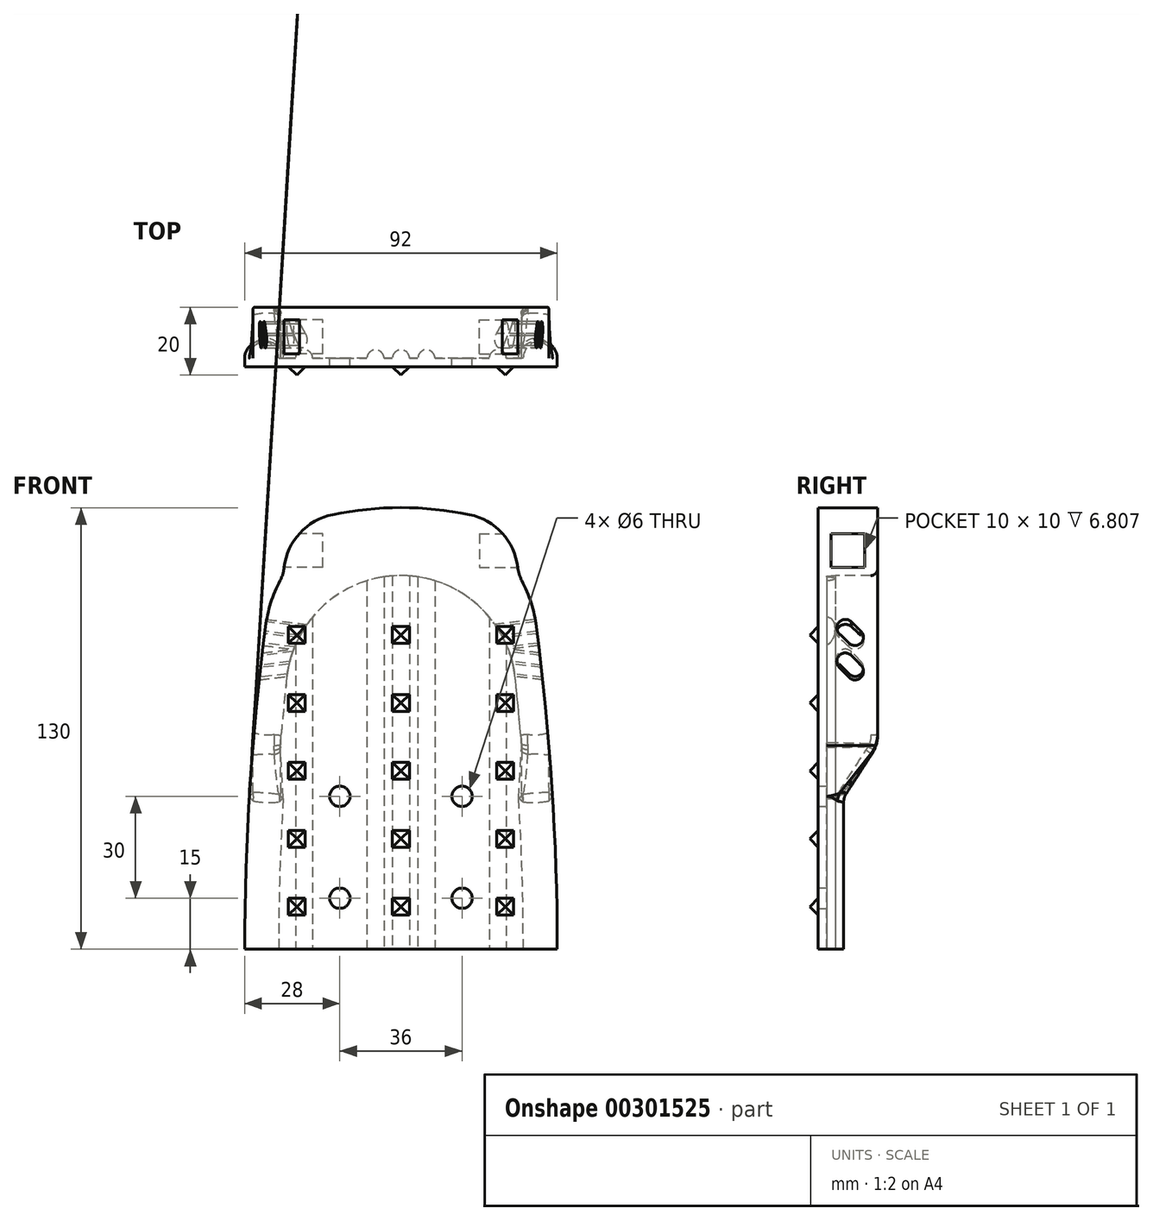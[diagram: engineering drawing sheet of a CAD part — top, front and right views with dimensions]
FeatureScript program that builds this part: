
annotation { "Feature Type Name" : "Feature", "Feature Type Description" : "" }
export const myFeature = defineFeature(function(context is Context, id is Id, definition is map)
    precondition{}
    {
        {
            assignVariable(context, id + "F0", {"name" : "Tb", "anyValue" : 2.5});
        }
        {
            assignVariable(context, id + "F1", {"name" : "tb2", "anyValue" : 15});
        }
        {
            var Q0;
            Q0=qCreatedBy(makeId("Front.planeOp"),FACE);
            var sketch = newSketch(context, id + "F2", { "sketchPlane" : qUnion([Q0])});
            skLineSegment(sketch, "E0", {"start": v(0, 0) * mm, "end": v(0, 130) * mm, "construction": true});
            skLineSegment(sketch, "E1", {"start": v(0, 0) * mm, "end": v(-41, 0) * mm});
            skLineSegment(sketch, "E2", {"start": v(0, 0) * mm, "end": v(46, 0) * mm});
            skLineSegment(sketch, "E3", {"start": v(0, 16) * mm, "end": v(-42, 16) * mm, "construction": true});
            skLineSegment(sketch, "E4", {"start": v(0, 16) * mm, "end": v(61, 16) * mm, "construction": true});
            skLineSegment(sketch, "E5", {"start": v(61, 26) * mm, "end": v(0, 26) * mm, "construction": true});
            skLineSegment(sketch, "E6", {"start": v(0, 26) * mm, "end": v(-43, 26) * mm, "construction": true});
            skLineSegment(sketch, "E7", {"start": v(-42, 46) * mm, "end": v(0, 46) * mm, "construction": true});
            skLineSegment(sketch, "E8", {"start": v(0, 46) * mm, "end": v(60, 46) * mm, "construction": true});
            skLineSegment(sketch, "E9", {"start": v(-40, 71) * mm, "end": v(0, 71) * mm, "construction": true});
            skLineSegment(sketch, "E10", {"start": v(0, 71) * mm, "end": v(53, 71) * mm, "construction": true});
            skLineSegment(sketch, "E11", {"start": v(-35, 97) * mm, "end": v(0, 97) * mm, "construction": true});
            skLineSegment(sketch, "E12", {"start": v(0, 97) * mm, "end": v(44, 97) * mm, "construction": true});
            skLineSegment(sketch, "E13", {"start": v(-29, 112) * mm, "end": v(0, 112) * mm, "construction": true});
            skLineSegment(sketch, "E14", {"start": v(0, 112) * mm, "end": v(35, 112) * mm, "construction": true});
            skArc(sketch, "E15", {"start": v(39.87, 94.96) * mm, "mid": v(26.54, 120) * mm, "end": v(0, 130) * mm});
            skPoint(sketch, "E16.visualSharp", {"position": v(-35, 97) * mm});
            skPoint(sketch, "E17.visualSharp", {"position": v(-40, 71) * mm});
            skPoint(sketch, "E18.visualSharp", {"position": v(-42, 46) * mm});
            skPoint(sketch, "E19.visualSharp", {"position": v(-43, 26) * mm});
            skPoint(sketch, "E20.visualSharp", {"position": v(-42, 16) * mm});
            skPoint(sketch, "E21.visualSharp", {"position": v(61, 16) * mm});
            skPoint(sketch, "E22.visualSharp", {"position": v(61, 26) * mm});
            skPoint(sketch, "E23.visualSharp", {"position": v(60, 46) * mm});
            skPoint(sketch, "E24.visualSharp", {"position": v(53, 71) * mm});
            skPoint(sketch, "E25.visualSharp", {"position": v(44, 97) * mm});
            skArc(sketch, "E26", {"start": v(46, 0) * mm, "mid": v(44.47, 47.58) * mm, "end": v(39.87, 94.96) * mm});
            skLineSegment(sketch, "E27", {"start": v(-41, 0) * mm, "end": v(-46, 0) * mm});
            skLineSegment(sketch, "E28", {"start": v(46, 0) * mm, "end": v(46, 0) * mm});
            skLineSegment(sketch, "E29", {"start": v(-27.54, 130) * mm, "end": v(25.43, 130) * mm, "construction": true});
            skArc(sketch, "E30.MirrorCS", {"start": v(-39.87, 94.96) * mm, "mid": v(-26.54, 120) * mm, "end": v(0, 130) * mm});
            skArc(sketch, "E31.MirrorCS", {"start": v(-46, 0) * mm, "mid": v(-44.47, 47.58) * mm, "end": v(-39.87, 94.96) * mm});
            skLineSegment(sketch, "E32", {"start": v(46, 0) * mm, "end": v(46, -31.18) * mm, "construction": true});
            skLineSegment(sketch, "E33", {"start": v(-80.2, 90) * mm, "end": v(120.58, 90) * mm, "construction": true});
            skPoint(sketch, "E34", {"position": v(40.5, 90) * mm});
            skSolve(sketch);
        }
        {
            var Q0;
            Q0=qSketchRegion(id+"F2",true);
            var Q1;
            {var subQ5=sQuery(id+"F2.wireOp",EDGE,"E4");Q1=makeQuery(id+"F2.imprint","IMPRINT",FACE,{"disambiguationData":[TD([[makeQuery(id+"F2.imprint","IMPRINT",EDGE,{"derivedFrom":subQ5}),1.0]])]});}
            var Q2;
            {var subQ2=sQuery(id+"F2.wireOp",EDGE,"E14");Q2=makeQuery(id+"F2.imprint","IMPRINT",FACE,{"disambiguationData":[TD([[makeQuery(id+"F2.imprint","IMPRINT",EDGE,{"derivedFrom":subQ2}),1.0]])]});}
            var Q3;
            {var subQ2=sQuery(id+"F2.wireOp",EDGE,"E13");Q3=makeQuery(id+"F2.imprint","IMPRINT",FACE,{"disambiguationData":[TD([[makeQuery(id+"F2.imprint","IMPRINT",EDGE,{"derivedFrom":subQ2}),1.0]])]});}
            var Q4;
            {var subQ5=sQuery(id+"F2.wireOp",EDGE,"E3");Q4=makeQuery(id+"F2.imprint","IMPRINT",FACE,{"disambiguationData":[TD([[makeQuery(id+"F2.imprint","IMPRINT",EDGE,{"derivedFrom":subQ5}),-1.0]])]});}
            var Q5;
            {var subQ0=sQuery(id+"F2.wireOp",EDGE,"E9");var subQ1=sQuery(id+"F2.wireOp",EDGE,"E0");var subQ2=makeQuery(id+"F2.imprint","INTERSECT",VERTEX,{"derivedFrom":[subQ1,subQ0]});Q5=makeQuery(id+"F2.imprint","IMPRINT",FACE,{"disambiguationData":[TD([[makeQuery(id+"F2.imprint","IMPRINT",EDGE,{"disambiguationData":[TD([[subQ2,-1.0]])],"derivedFrom":subQ1}),1.0]])]});}
            var Q6;
            {var subQ3=sQuery(id+"F2.wireOp",EDGE,"E13");Q6=makeQuery(id+"F2.imprint","IMPRINT",FACE,{"disambiguationData":[TD([[makeQuery(id+"F2.imprint","IMPRINT",EDGE,{"derivedFrom":subQ3}),-1.0]])]});}
            var Q7;
            {var subQ1=sQuery(id+"F2.wireOp",EDGE,"E0");var subQ5=makeQuery(id+"F2.imprint","IMPRINT",VERTEX,{"derivedFrom":subQ1});Q7=makeQuery(id+"F2.imprint","IMPRINT",FACE,{"disambiguationData":[TD([[makeQuery(id+"F2.imprint","IMPRINT",EDGE,{"disambiguationData":[TD([[subQ5,1.0]])],"derivedFrom":subQ1}),1.0]])]});}
            extrude(context, id + "F3", {"entities" : qUnion([Q0, Q1, Q2, Q3, Q4, Q5, Q6, Q7]), "depth" : (getVariable(context, 'Tb')) * mm});
        }
        {
            var Q0;
            Q0=makeQuery(id+"F3.opExtrude","CAP_FACE",FACE,{"disambiguationData":[OSD([sQuery(id+"F2.wireOp",EDGE,"E1"),sQuery(id+"F2.wireOp",EDGE,"E2"),sQuery(id+"F2.wireOp",EDGE,"E15"),sQuery(id+"F2.wireOp",EDGE,"E26"),sQuery(id+"F2.wireOp",EDGE,"E27"),sQuery(id+"F2.wireOp",EDGE,"E30.MirrorCS"),sQuery(id+"F2.wireOp",EDGE,"E31.MirrorCS")])],"isStart":true});
            var sketch = newSketch(context, id + "F4", { "sketchPlane" : qUnion([Q0])});
            skArc(sketch, "E35.0", {"start": v(39.87, 94.96) * mm, "mid": v(0, 130) * mm, "end": v(-39.87, 94.96) * mm});
            skArc(sketch, "E36.0", {"start": v(-43.56, 60) * mm, "mid": v(-41.93, 77.5) * mm, "end": v(-39.87, 94.96) * mm});
            skArc(sketch, "E37.0", {"start": v(43.56, 60) * mm, "mid": v(41.93, 77.5) * mm, "end": v(39.87, 94.96) * mm});
            skPoint(sketch, "E38", {"position": v(0, 130) * mm});
            skArc(sketch, "E39.0", {"start": v(-35.53, 60) * mm, "mid": v(-34.65, 69.94) * mm, "end": v(-33.62, 79.87) * mm});
            skArc(sketch, "E40.0", {"start": v(35.53, 60) * mm, "mid": v(34.65, 69.94) * mm, "end": v(33.62, 79.87) * mm});
            skArc(sketch, "E41", {"start": v(33.62, 79.87) * mm, "mid": v(0, 110) * mm, "end": v(-33.62, 79.87) * mm});
            skPoint(sketch, "E42", {"position": v(0, 110) * mm});
            skLineSegment(sketch, "E43", {"start": v(-43.56, 60) * mm, "end": v(-35.53, 60) * mm});
            skLineSegment(sketch, "E44", {"start": v(35.53, 60) * mm, "end": v(43.56, 60) * mm});
            skSolve(sketch);
        }
        {
            var Q0;
            Q0 = qSketchRegion(id + "F4", true);
            extrude(context, id + "F5", {"entities" : qUnion([Q0]), "operationType" : NewBodyOperationType.ADD, "depth" : (getVariable(context, 'tb2')) * mm});
        }
        {
            var Q0;
            Q0=makeQuery(id+"F5.opExtrude","CAP_FACE",FACE,{"disambiguationData":[OSD([sQuery(id+"F4.wireOp",EDGE,"E35.0"),sQuery(id+"F4.wireOp",EDGE,"E36.0"),sQuery(id+"F4.wireOp",EDGE,"E37.0"),sQuery(id+"F4.wireOp",EDGE,"E39.0"),sQuery(id+"F4.wireOp",EDGE,"E40.0"),sQuery(id+"F4.wireOp",EDGE,"E41"),sQuery(id+"F4.wireOp",EDGE,"E43"),sQuery(id+"F4.wireOp",EDGE,"E44")])],"isStart":false});
            var sketch = newSketch(context, id + "F6", { "sketchPlane" : qUnion([Q0])});
            skLineSegment(sketch, "E45", {"start": v(0, 0) * mm, "end": v(0, 130) * mm, "construction": true});
            skArc(sketch, "E46.0", {"start": v(39.87, 94.96) * mm, "mid": v(0, 130) * mm, "end": v(-39.87, 94.96) * mm});
            skPoint(sketch, "E47", {"position": v(-33.06, 117.38) * mm});
            skPoint(sketch, "E48", {"position": v(33.06, 117.38) * mm});
            skPoint(sketch, "E49", {"position": v(0, 65) * mm});
            skArc(sketch, "E50", {"start": v(-20.12, 127.95) * mm, "mid": v(-29.78, 122.48) * mm, "end": v(-34.38, 112.38) * mm});
            skArc(sketch, "E51", {"start": v(0, 130) * mm, "mid": v(-10.11, 129.49) * mm, "end": v(-20.12, 127.95) * mm});
            skLineSegment(sketch, "E52", {"start": v(-37.94, 130) * mm, "end": v(-5.5, 130) * mm, "construction": true});
            skPoint(sketch, "E53", {"position": v(0, 130) * mm});
            skArc(sketch, "E54.MirrorCS", {"start": v(0, 130) * mm, "mid": v(10.11, 129.49) * mm, "end": v(20.12, 127.95) * mm});
            skArc(sketch, "E55.MirrorCS", {"start": v(20.12, 127.95) * mm, "mid": v(29.78, 122.48) * mm, "end": v(34.38, 112.38) * mm});
            skArc(sketch, "E56.0", {"start": v(-43.56, 60) * mm, "mid": v(-41.78, 78.84) * mm, "end": v(-39.52, 97.64) * mm});
            skArc(sketch, "E57.0", {"start": v(-43.56, 60) * mm, "mid": v(-41.93, 77.5) * mm, "end": v(-39.87, 94.96) * mm});
            skArc(sketch, "E58.0", {"start": v(43.56, 60) * mm, "mid": v(41.93, 77.5) * mm, "end": v(39.87, 94.96) * mm});
            skArc(sketch, "E59", {"start": v(34.38, 112.38) * mm, "mid": v(34.8, 110.4) * mm, "end": v(35.57, 108.54) * mm});
            skArc(sketch, "E60.MirrorCS", {"start": v(-34.38, 112.38) * mm, "mid": v(-34.8, 110.4) * mm, "end": v(-35.57, 108.54) * mm});
            skSolve(sketch);
        }
        {
            var Q0;
            Q0 = qSketchRegion(id + "F6", true);
            var Q1;
            {var subQ0=sQuery(id+"F10.wireOp",EDGE,"E70.4.0.0");var subQ1=sQuery(id+"F2.wireOp",EDGE,"E27");var subQ2=sQuery(id+"F2.wireOp",EDGE,"E2");var subQ3=sQuery(id+"F2.wireOp",EDGE,"E1");var subQ4=sQuery(id+"F9.wireOp",EDGE,"E65");var subQ5=sQuery(id+"F9.wireOp",EDGE,"E64");var subQ6=sQuery(id+"F10.wireOp",EDGE,"E70.5.0.0");Q1=makeQuery(id+"FkjtFRoMZpxTrFz_1.boolean.opBoolean","SPLIT",FACE,{"disambiguationData":[TD([makeQuery(id+"F3.opExtrude","SWEPT_FACE",FACE,{"disambiguationData":[OSD([subQ3,subQ2,subQ1])]}),makeQuery(id+"FU9GR2EhDPic5YP_1.opSweep","CAP_FACE",FACE,{"disambiguationData":[OSD([sQuery(id+"F8.wireOp",VERTEX,"E61.0.start"),subQ5,subQ4])],"isStart":true}),makeQuery(id+"FU9GR2EhDPic5YP_1.opSweep","CAP_FACE",FACE,{"disambiguationData":[OSD([sQuery(id+"F8.wireOp",VERTEX,"E63.0.start"),subQ5,subQ4])],"isStart":false}),makeQuery(id+"FU9GR2EhDPic5YP_1.opSweep","SWEPT_FACE",FACE,{"disambiguationData":[OSD([sQuery(id+"F8.wireOp",EDGE,"E62.0"),subQ5])]}),makeQuery(id+"FkjtFRoMZpxTrFz_1.opExtrude","CAP_FACE",FACE,{"disambiguationData":[OSD([sQuery(id+"F10.wireOp",EDGE,"E66"),sQuery(id+"F10.wireOp",EDGE,"E67")])],"isStart":true}),makeQuery(id+"FkjtFRoMZpxTrFz_1.opExtrude","CAP_FACE",FACE,{"disambiguationData":[OSD([sQuery(id+"F10.wireOp",EDGE,"E70.1.0.0"),sQuery(id+"F10.wireOp",EDGE,"E70.1.0.1")])],"isStart":true}),makeQuery(id+"FkjtFRoMZpxTrFz_1.opExtrude","CAP_FACE",FACE,{"disambiguationData":[OSD([sQuery(id+"F10.wireOp",EDGE,"E70.2.0.0"),sQuery(id+"F10.wireOp",EDGE,"E70.2.0.1")])],"isStart":true}),makeQuery(id+"FkjtFRoMZpxTrFz_1.opExtrude","CAP_FACE",FACE,{"disambiguationData":[OSD([sQuery(id+"F10.wireOp",EDGE,"E70.3.0.0"),sQuery(id+"F10.wireOp",EDGE,"E70.3.0.1")])],"isStart":true}),makeQuery(id+"FkjtFRoMZpxTrFz_1.opExtrude","SWEPT_FACE",FACE,{"disambiguationData":[OSD([subQ0])]}),makeQuery(id+"FkjtFRoMZpxTrFz_1.opExtrude","CAP_FACE",FACE,{"disambiguationData":[OSD([subQ0,sQuery(id+"F10.wireOp",EDGE,"E70.4.0.1")])],"isStart":true}),makeQuery(id+"FkjtFRoMZpxTrFz_1.opExtrude","SWEPT_FACE",FACE,{"disambiguationData":[OSD([subQ6])]}),makeQuery(id+"FkjtFRoMZpxTrFz_1.opExtrude","CAP_FACE",FACE,{"disambiguationData":[OSD([subQ6,sQuery(id+"F10.wireOp",EDGE,"E70.5.0.1")])],"isStart":true}),makeQuery(id+"FkjtFRoMZpxTrFz_1.opExtrude","CAP_FACE",FACE,{"disambiguationData":[OSD([sQuery(id+"F10.wireOp",EDGE,"E70.6.0.0"),sQuery(id+"F10.wireOp",EDGE,"E70.6.0.1")])],"isStart":true}),makeQuery(id+"FkjtFRoMZpxTrFz_1.opExtrude","CAP_FACE",FACE,{"disambiguationData":[OSD([sQuery(id+"F10.wireOp",EDGE,"E70.7.0.0"),sQuery(id+"F10.wireOp",EDGE,"E70.7.0.1")])],"isStart":true})])],"derivedFrom":makeQuery(id+"F3.opExtrude","CAP_FACE",FACE,{"disambiguationData":[OSD([subQ3,subQ2,sQuery(id+"F2.wireOp",EDGE,"E15"),sQuery(id+"F2.wireOp",EDGE,"E26"),subQ1,sQuery(id+"F2.wireOp",EDGE,"E30.MirrorCS"),sQuery(id+"F2.wireOp",EDGE,"E31.MirrorCS")])],"isStart":false})});}
            extrude(context, id + "F7", {"entities" : qUnion([Q0]), "operationType" : NewBodyOperationType.ADD, "endBound" : BoundingType.UP_TO_SURFACE, "oppositeDirection" : true, "endBoundEntityFace" : qUnion([Q1]), "depth" : 25 * mm});
        }
        {
            var Q0;
            Q0=makeQuery(id+"F3.opExtrude","CAP_FACE",FACE,{"disambiguationData":[OSD([sQuery(id+"F2.wireOp",EDGE,"E1"),sQuery(id+"F2.wireOp",EDGE,"E2"),sQuery(id+"F2.wireOp",EDGE,"E15"),sQuery(id+"F2.wireOp",EDGE,"E26"),sQuery(id+"F2.wireOp",EDGE,"E27"),sQuery(id+"F2.wireOp",EDGE,"E30.MirrorCS"),sQuery(id+"F2.wireOp",EDGE,"E31.MirrorCS")])],"isStart":false});
            var sketch = newSketch(context, id + "F8", { "sketchPlane" : qUnion([Q0])});
            skArc(sketch, "E61.0", {"start": v(-46, 0) * mm, "mid": v(-44.47, 47.58) * mm, "end": v(-39.87, 94.96) * mm});
            skArc(sketch, "E62.0", {"start": v(-39.87, 94.96) * mm, "mid": v(0, 130) * mm, "end": v(39.87, 94.96) * mm});
            skArc(sketch, "E63.0", {"start": v(46, 0) * mm, "mid": v(44.47, 47.58) * mm, "end": v(39.87, 94.96) * mm});
            skSolve(sketch);
        }
        {
            var Q0;
            Q0=makeQuery(id+"F3.opExtrude","SWEPT_FACE",FACE,{"disambiguationData":[OSD([sQuery(id+"F2.wireOp",EDGE,"E1"),sQuery(id+"F2.wireOp",EDGE,"E2"),sQuery(id+"F2.wireOp",EDGE,"E27")])]});
            var sketch = newSketch(context, id + "F9", { "sketchPlane" : qUnion([Q0])});
            skArc(sketch, "E64", {"start": v(-40, 2.5) * mm, "mid": v(-43, 5.5) * mm, "end": v(-46, 2.5) * mm});
            skLineSegment(sketch, "E65", {"start": v(-46, 2.5) * mm, "end": v(-40, 2.5) * mm});
            skSolve(sketch);
        }
        {
            var Q0;
            Q0=makeQuery(id+"FU9GR2EhDPic5YP_1.boolean.opBoolean","MERGE",FACE,{"derivedFrom":[makeQuery(id+"F3.opExtrude","SWEPT_FACE",FACE,{"disambiguationData":[OSD([sQuery(id+"F2.wireOp",EDGE,"E1"),sQuery(id+"F2.wireOp",EDGE,"E2"),sQuery(id+"F2.wireOp",EDGE,"E27")])]}),makeQuery(id+"FU9GR2EhDPic5YP_1.opSweep","CAP_FACE",FACE,{"disambiguationData":[OSD([sQuery(id+"F8.wireOp",VERTEX,"E61.0.start"),sQuery(id+"F9.wireOp",EDGE,"E64"),sQuery(id+"F9.wireOp",EDGE,"E65")])],"isStart":true})]});
            var sketch = newSketch(context, id + "F10", { "sketchPlane" : qUnion([Q0])});
            skArc(sketch, "E66", {"start": v(-31, 2.5) * mm, "mid": v(-33.5, 5) * mm, "end": v(-36, 2.5) * mm});
            skLineSegment(sketch, "E67", {"start": v(-36, 2.5) * mm, "end": v(-31, 2.5) * mm});
            skPoint(sketch, "E68.0", {"position": v(-46, 2.5) * mm});
            skPoint(sketch, "E69.0", {"position": v(46, 2.5) * mm});
            skArc(sketch, "E70.1.0.0", {"start": v(-21.43, 2.5) * mm, "mid": v(-23.93, 5) * mm, "end": v(-26.43, 2.5) * mm});
            skLineSegment(sketch, "E70.1.0.1", {"start": v(-26.43, 2.5) * mm, "end": v(-21.43, 2.5) * mm});
            skArc(sketch, "E70.2.0.0", {"start": v(-11.86, 2.5) * mm, "mid": v(-14.36, 5) * mm, "end": v(-16.86, 2.5) * mm});
            skLineSegment(sketch, "E70.2.0.1", {"start": v(-16.86, 2.5) * mm, "end": v(-11.86, 2.5) * mm});
            skArc(sketch, "E70.3.0.0", {"start": v(-2.29, 2.5) * mm, "mid": v(-4.79, 5) * mm, "end": v(-7.29, 2.5) * mm});
            skLineSegment(sketch, "E70.3.0.1", {"start": v(-7.29, 2.5) * mm, "end": v(-2.29, 2.5) * mm});
            skArc(sketch, "E70.4.0.0", {"start": v(7.29, 2.5) * mm, "mid": v(4.79, 5) * mm, "end": v(2.29, 2.5) * mm});
            skLineSegment(sketch, "E70.4.0.1", {"start": v(2.29, 2.5) * mm, "end": v(7.29, 2.5) * mm});
            skArc(sketch, "E70.5.0.0", {"start": v(16.86, 2.5) * mm, "mid": v(14.36, 5) * mm, "end": v(11.86, 2.5) * mm});
            skLineSegment(sketch, "E70.5.0.1", {"start": v(11.86, 2.5) * mm, "end": v(16.86, 2.5) * mm});
            skArc(sketch, "E70.6.0.0", {"start": v(26.43, 2.5) * mm, "mid": v(23.93, 5) * mm, "end": v(21.43, 2.5) * mm});
            skLineSegment(sketch, "E70.6.0.1", {"start": v(21.43, 2.5) * mm, "end": v(26.43, 2.5) * mm});
            skArc(sketch, "E70.7.0.0", {"start": v(36, 2.5) * mm, "mid": v(33.5, 5) * mm, "end": v(31, 2.5) * mm});
            skLineSegment(sketch, "E70.7.0.1", {"start": v(31, 2.5) * mm, "end": v(36, 2.5) * mm});
            skLineSegment(sketch, "E70.direction1", {"start": v(-36, 2.5) * mm, "end": v(-26.43, 2.5) * mm, "construction": true});
            skLineSegment(sketch, "E71", {"start": v(36, 2.5) * mm, "end": v(46, 2.5) * mm, "construction": true});
            skLineSegment(sketch, "E72", {"start": v(-36, 2.5) * mm, "end": v(-46, 2.5) * mm, "construction": true});
            skSolve(sketch);
        }
        {
            var Q0;
            {var subQ0=sQuery(id+"F6.wireOp",EDGE,"E46.0");Q0=makeQuery(id+"F7.boolean.opBoolean","MERGE",FACE,{"derivedFrom":[makeQuery(id+"F5.opExtrude","CAP_FACE",FACE,{"disambiguationData":[OSD([sQuery(id+"F4.wireOp",EDGE,"E35.0"),sQuery(id+"F4.wireOp",EDGE,"E36.0"),sQuery(id+"F4.wireOp",EDGE,"E37.0"),sQuery(id+"F4.wireOp",EDGE,"E39.0"),sQuery(id+"F4.wireOp",EDGE,"E40.0"),sQuery(id+"F4.wireOp",EDGE,"E41"),sQuery(id+"F4.wireOp",EDGE,"E43"),sQuery(id+"F4.wireOp",EDGE,"E44")])],"isStart":false}),makeQuery(id+"F7.opExtrude","CAP_FACE",FACE,{"disambiguationData":[OSD([subQ0,sQuery(id+"F6.wireOp",EDGE,"E54.MirrorCS"),sQuery(id+"F6.wireOp",EDGE,"E55.MirrorCS"),sQuery(id+"F6.wireOp",EDGE,"E59")])],"isStart":true}),makeQuery(id+"F7.opExtrude","CAP_FACE",FACE,{"disambiguationData":[OSD([subQ0,sQuery(id+"F6.wireOp",EDGE,"E50"),sQuery(id+"F6.wireOp",EDGE,"E51"),sQuery(id+"F6.wireOp",EDGE,"E60.MirrorCS")])],"isStart":true})]});}
            var sketch = newSketch(context, id + "F11", { "sketchPlane" : qUnion([Q0])});
            skPoint(sketch, "E73.0", {"position": v(-33.06, 117.38) * mm});
            skPoint(sketch, "E74.0", {"position": v(33.06, 117.38) * mm});
            skSolve(sketch);
        }
        {
            var Q0;
            Q0=qCreatedBy(makeId("Right.planeOp"),FACE);
            var Q1;
            Q1=sQuery(id+"F11.wireOp",VERTEX,"E73.0");
            cPlane(context, id + "F12", {"entities" : qUnion([Q0, Q1]), "cplaneType" : CPlaneType.PLANE_POINT, "offset" : 25 * mm, "width" : 150 * mm, "height" : 150 * mm});
        }
        {
            var Q0;
            Q0=sQuery(id+"F11.wireOp",VERTEX,"E74.0");
            var Q1;
            Q1=qCreatedBy(makeId("Right.planeOp"),FACE);
            cPlane(context, id + "F13", {"entities" : qUnion([Q0, Q1]), "cplaneType" : CPlaneType.PLANE_POINT, "offset" : 25 * mm, "width" : 150 * mm, "height" : 150 * mm});
        }
        {
            var Q0;
            Q0=qCreatedBy(id+"F13.planeOp",FACE);
            var sketch = newSketch(context, id + "F14", { "sketchPlane" : qUnion([Q0])});
            skLineSegment(sketch, "E75", {"start": v(15, 117.38) * mm, "end": v(-2.5, 117.38) * mm, "construction": true});
            skPoint(sketch, "E76", {"position": v(6.25, 117.38) * mm});
            skLineSegment(sketch, "E77.bottom", {"start": v(1.25, 112.38) * mm, "end": v(11.25, 112.38) * mm});
            skLineSegment(sketch, "E77.top", {"start": v(1.25, 122.38) * mm, "end": v(11.25, 122.38) * mm});
            skLineSegment(sketch, "E77.left", {"start": v(1.25, 112.38) * mm, "end": v(1.25, 122.38) * mm});
            skLineSegment(sketch, "E77.right", {"start": v(11.25, 112.38) * mm, "end": v(11.25, 122.38) * mm});
            skSolve(sketch);
        }
        {
            var Q0;
            Q0 = qSketchRegion(id + "F14", true);
            extrude(context, id + "F15", {"entities" : qUnion([Q0]), "operationType" : NewBodyOperationType.REMOVE, "depth" : 10 * mm, "hasSecondDirection" : true, "secondDirectionOppositeDirection" : true, "secondDirectionDepth" : 25 * mm});
        }
        {
            var Q0;
            Q0=qCreatedBy(id+"F12.planeOp",FACE);
            var sketch = newSketch(context, id + "F16", { "sketchPlane" : qUnion([Q0])});
            skLineSegment(sketch, "E78", {"start": v(15, 117.38) * mm, "end": v(-2.5, 117.38) * mm, "construction": true});
            skPoint(sketch, "E79", {"position": v(6.25, 117.38) * mm});
            skLineSegment(sketch, "E80.bottom", {"start": v(1.25, 122.38) * mm, "end": v(11.25, 122.38) * mm});
            skLineSegment(sketch, "E80.top", {"start": v(1.25, 112.38) * mm, "end": v(11.25, 112.38) * mm});
            skLineSegment(sketch, "E80.left", {"start": v(1.25, 122.38) * mm, "end": v(1.25, 112.38) * mm});
            skLineSegment(sketch, "E80.right", {"start": v(11.25, 122.38) * mm, "end": v(11.25, 112.38) * mm});
            skSolve(sketch);
        }
        {
            var Q0;
            Q0=makeQuery(id+"F16.imprint","IMPRINT",FACE,{"disambiguationData":[TD([[makeQuery(id+"F16.imprint","IMPRINT",EDGE,{"derivedFrom":sQuery(id+"F16.wireOp",EDGE,"E80.bottom")}),-1.0]])]});
            extrude(context, id + "F17", {"entities" : qUnion([Q0]), "operationType" : NewBodyOperationType.REMOVE, "oppositeDirection" : true, "depth" : 10 * mm, "hasSecondDirection" : true, "secondDirectionOppositeDirection" : false, "secondDirectionDepth" : 25 * mm});
        }
        {
            var Q0;
            Q0=makeQuery(id+"F3.opExtrude","CAP_FACE",FACE,{"disambiguationData":[OSD([sQuery(id+"F2.wireOp",EDGE,"E1"),sQuery(id+"F2.wireOp",EDGE,"E2"),sQuery(id+"F2.wireOp",EDGE,"E15"),sQuery(id+"F2.wireOp",EDGE,"E26"),sQuery(id+"F2.wireOp",EDGE,"E27"),sQuery(id+"F2.wireOp",EDGE,"E30.MirrorCS"),sQuery(id+"F2.wireOp",EDGE,"E31.MirrorCS")])],"isStart":true});
            var sketch = newSketch(context, id + "F18", { "sketchPlane" : qUnion([Q0])});
            skArc(sketch, "E81.0", {"start": v(46, 0) * mm, "mid": v(45.66, 22.51) * mm, "end": v(44.63, 45) * mm});
            skArc(sketch, "E82.0", {"start": v(-46, 0) * mm, "mid": v(-45.66, 22.51) * mm, "end": v(-44.63, 45) * mm});
            skSolve(sketch);
        }
        {
            var Q0;
            {var subQ0=sQuery(id+"F9.wireOp",EDGE,"E65");var subQ1=sQuery(id+"F9.wireOp",EDGE,"E64");Q0=makeQuery(id+"FkjtFRoMZpxTrFz_1.boolean.opBoolean","MERGE",FACE,{"derivedFrom":[makeQuery(id+"FU9GR2EhDPic5YP_1.boolean.opBoolean","MERGE",FACE,{"derivedFrom":[makeQuery(id+"F3.opExtrude","SWEPT_FACE",FACE,{"disambiguationData":[OSD([sQuery(id+"F2.wireOp",EDGE,"E1"),sQuery(id+"F2.wireOp",EDGE,"E2"),sQuery(id+"F2.wireOp",EDGE,"E27")])]}),makeQuery(id+"FU9GR2EhDPic5YP_1.opSweep","CAP_FACE",FACE,{"disambiguationData":[OSD([sQuery(id+"F8.wireOp",VERTEX,"E61.0.start"),subQ1,subQ0])],"isStart":true}),makeQuery(id+"FU9GR2EhDPic5YP_1.opSweep","CAP_FACE",FACE,{"disambiguationData":[OSD([sQuery(id+"F8.wireOp",VERTEX,"E63.0.start"),subQ1,subQ0])],"isStart":false})]}),makeQuery(id+"FkjtFRoMZpxTrFz_1.opExtrude","CAP_FACE",FACE,{"disambiguationData":[OSD([sQuery(id+"F10.wireOp",EDGE,"E66"),sQuery(id+"F10.wireOp",EDGE,"E67")])],"isStart":true}),makeQuery(id+"FkjtFRoMZpxTrFz_1.opExtrude","CAP_FACE",FACE,{"disambiguationData":[OSD([sQuery(id+"F10.wireOp",EDGE,"E70.1.0.0"),sQuery(id+"F10.wireOp",EDGE,"E70.1.0.1")])],"isStart":true}),makeQuery(id+"FkjtFRoMZpxTrFz_1.opExtrude","CAP_FACE",FACE,{"disambiguationData":[OSD([sQuery(id+"F10.wireOp",EDGE,"E70.2.0.0"),sQuery(id+"F10.wireOp",EDGE,"E70.2.0.1")])],"isStart":true}),makeQuery(id+"FkjtFRoMZpxTrFz_1.opExtrude","CAP_FACE",FACE,{"disambiguationData":[OSD([sQuery(id+"F10.wireOp",EDGE,"E70.3.0.0"),sQuery(id+"F10.wireOp",EDGE,"E70.3.0.1")])],"isStart":true}),makeQuery(id+"FkjtFRoMZpxTrFz_1.opExtrude","CAP_FACE",FACE,{"disambiguationData":[OSD([sQuery(id+"F10.wireOp",EDGE,"E70.4.0.0"),sQuery(id+"F10.wireOp",EDGE,"E70.4.0.1")])],"isStart":true}),makeQuery(id+"FkjtFRoMZpxTrFz_1.opExtrude","CAP_FACE",FACE,{"disambiguationData":[OSD([sQuery(id+"F10.wireOp",EDGE,"E70.5.0.0"),sQuery(id+"F10.wireOp",EDGE,"E70.5.0.1")])],"isStart":true}),makeQuery(id+"FkjtFRoMZpxTrFz_1.opExtrude","CAP_FACE",FACE,{"disambiguationData":[OSD([sQuery(id+"F10.wireOp",EDGE,"E70.6.0.0"),sQuery(id+"F10.wireOp",EDGE,"E70.6.0.1")])],"isStart":true}),makeQuery(id+"FkjtFRoMZpxTrFz_1.opExtrude","CAP_FACE",FACE,{"disambiguationData":[OSD([sQuery(id+"F10.wireOp",EDGE,"E70.7.0.0"),sQuery(id+"F10.wireOp",EDGE,"E70.7.0.1")])],"isStart":true})]});}
            var sketch = newSketch(context, id + "F19", { "sketchPlane" : qUnion([Q0])});
            skArc(sketch, "E83", {"start": v(36, 0) * mm, "mid": v(41, -5) * mm, "end": v(46, 0) * mm});
            skLineSegment(sketch, "E84", {"start": v(46, 0) * mm, "end": v(36, 0) * mm});
            skSolve(sketch);
        }
        {
            var Q0;
            Q0=makeQuery(id+"F19.imprint","IMPRINT",FACE,{"disambiguationData":[TD([[makeQuery(id+"F19.imprint","IMPRINT",EDGE,{"derivedFrom":sQuery(id+"F19.wireOp",EDGE,"E83")}),1.0]])]});
            var Q1;
            Q1=sQuery(id+"F18.wireOp",EDGE,"E82.0");
            sweep(context, id + "F20", {"operationType" : NewBodyOperationType.ADD, "profiles" : qUnion([Q0]), "path" : qUnion([Q1])});
        }
        {
            var Q0;
            {var subQ0=sQuery(id+"F9.wireOp",EDGE,"E65");var subQ1=sQuery(id+"F9.wireOp",EDGE,"E64");Q0=makeQuery(id+"F20.boolean.opBoolean","MERGE",FACE,{"derivedFrom":[makeQuery(id+"FkjtFRoMZpxTrFz_1.boolean.opBoolean","MERGE",FACE,{"derivedFrom":[makeQuery(id+"FU9GR2EhDPic5YP_1.boolean.opBoolean","MERGE",FACE,{"derivedFrom":[makeQuery(id+"F3.opExtrude","SWEPT_FACE",FACE,{"disambiguationData":[OSD([sQuery(id+"F2.wireOp",EDGE,"E1"),sQuery(id+"F2.wireOp",EDGE,"E2"),sQuery(id+"F2.wireOp",EDGE,"E27")])]}),makeQuery(id+"FU9GR2EhDPic5YP_1.opSweep","CAP_FACE",FACE,{"disambiguationData":[OSD([sQuery(id+"F8.wireOp",VERTEX,"E61.0.start"),subQ1,subQ0])],"isStart":true}),makeQuery(id+"FU9GR2EhDPic5YP_1.opSweep","CAP_FACE",FACE,{"disambiguationData":[OSD([sQuery(id+"F8.wireOp",VERTEX,"E63.0.start"),subQ1,subQ0])],"isStart":false})]}),makeQuery(id+"FkjtFRoMZpxTrFz_1.opExtrude","CAP_FACE",FACE,{"disambiguationData":[OSD([sQuery(id+"F10.wireOp",EDGE,"E66"),sQuery(id+"F10.wireOp",EDGE,"E67")])],"isStart":true}),makeQuery(id+"FkjtFRoMZpxTrFz_1.opExtrude","CAP_FACE",FACE,{"disambiguationData":[OSD([sQuery(id+"F10.wireOp",EDGE,"E70.1.0.0"),sQuery(id+"F10.wireOp",EDGE,"E70.1.0.1")])],"isStart":true}),makeQuery(id+"FkjtFRoMZpxTrFz_1.opExtrude","CAP_FACE",FACE,{"disambiguationData":[OSD([sQuery(id+"F10.wireOp",EDGE,"E70.2.0.0"),sQuery(id+"F10.wireOp",EDGE,"E70.2.0.1")])],"isStart":true}),makeQuery(id+"FkjtFRoMZpxTrFz_1.opExtrude","CAP_FACE",FACE,{"disambiguationData":[OSD([sQuery(id+"F10.wireOp",EDGE,"E70.3.0.0"),sQuery(id+"F10.wireOp",EDGE,"E70.3.0.1")])],"isStart":true}),makeQuery(id+"FkjtFRoMZpxTrFz_1.opExtrude","CAP_FACE",FACE,{"disambiguationData":[OSD([sQuery(id+"F10.wireOp",EDGE,"E70.4.0.0"),sQuery(id+"F10.wireOp",EDGE,"E70.4.0.1")])],"isStart":true}),makeQuery(id+"FkjtFRoMZpxTrFz_1.opExtrude","CAP_FACE",FACE,{"disambiguationData":[OSD([sQuery(id+"F10.wireOp",EDGE,"E70.5.0.0"),sQuery(id+"F10.wireOp",EDGE,"E70.5.0.1")])],"isStart":true}),makeQuery(id+"FkjtFRoMZpxTrFz_1.opExtrude","CAP_FACE",FACE,{"disambiguationData":[OSD([sQuery(id+"F10.wireOp",EDGE,"E70.6.0.0"),sQuery(id+"F10.wireOp",EDGE,"E70.6.0.1")])],"isStart":true}),makeQuery(id+"FkjtFRoMZpxTrFz_1.opExtrude","CAP_FACE",FACE,{"disambiguationData":[OSD([sQuery(id+"F10.wireOp",EDGE,"E70.7.0.0"),sQuery(id+"F10.wireOp",EDGE,"E70.7.0.1")])],"isStart":true})]}),makeQuery(id+"F20.opSweep","CAP_FACE",FACE,{"disambiguationData":[OSD([sQuery(id+"F18.wireOp",VERTEX,"137de014-e79f-42d4-9166-d3d45082f0f9.0.start"),sQuery(id+"F19.wireOp",EDGE,"E83"),sQuery(id+"F19.wireOp",EDGE,"E84")])],"isStart":true})]});}
            var sketch = newSketch(context, id + "F21", { "sketchPlane" : qUnion([Q0])});
            skArc(sketch, "E85", {"start": v(-46, 0) * mm, "mid": v(-41, -5) * mm, "end": v(-36, 0) * mm});
            skLineSegment(sketch, "E86", {"start": v(-46, 0) * mm, "end": v(-36, 0) * mm});
            skSolve(sketch);
        }
        {
            var Q0;
            Q0=makeQuery(id+"F21.imprint","IMPRINT",FACE,{"disambiguationData":[TD([[makeQuery(id+"F21.imprint","IMPRINT",EDGE,{"derivedFrom":sQuery(id+"F21.wireOp",EDGE,"E85")}),1.0]])]});
            var Q1;
            Q1=sQuery(id+"F18.wireOp",EDGE,"E81.0");
            sweep(context, id + "F22", {"operationType" : NewBodyOperationType.ADD, "profiles" : qUnion([Q0]), "path" : qUnion([Q1])});
        }
        {
            var Q0;
            Q0=makeQuery(id+"F5.opExtrude","SWEPT_FACE",FACE,{"disambiguationData":[OSD([sQuery(id+"F4.wireOp",EDGE,"E44")])]});
            var sketch = newSketch(context, id + "F23", { "sketchPlane" : qUnion([Q0])});
            skLineSegment(sketch, "E87.0", {"start": v(-35.53, -15) * mm, "end": v(-43.56, -15) * mm});
            skLineSegment(sketch, "E88.0", {"start": v(-43.56, -15) * mm, "end": v(-43.56, 0) * mm});
            skLineSegment(sketch, "E89.0", {"start": v(-35.53, -15) * mm, "end": v(-35.53, 0) * mm});
            skLineSegment(sketch, "E90", {"start": v(-43.56, 0) * mm, "end": v(-35.53, 0) * mm});
            skSolve(sketch);
        }
        {
            var Q0;
            Q0=makeQuery(id+"F22.opSweep","CAP_FACE",FACE,{"disambiguationData":[OSD([sQuery(id+"F18.wireOp",VERTEX,"E81.0.end"),sQuery(id+"F21.wireOp",EDGE,"E85"),sQuery(id+"F21.wireOp",EDGE,"E86")])],"isStart":false});
            var sketch = newSketch(context, id + "F24", { "sketchPlane" : qUnion([Q0])});
            skLineSegment(sketch, "E91.0", {"start": v(-47.29, 0) * mm, "end": v(-37.29, 0) * mm});
            skPoint(sketch, "E92", {"position": v(-46.29, 3) * mm});
            skPoint(sketch, "E93", {"position": v(-38.29, 3) * mm});
            skArc(sketch, "E94", {"start": v(-46.29, 3) * mm, "mid": v(-47.03, 1.58) * mm, "end": v(-47.29, 0) * mm});
            skArc(sketch, "E95", {"start": v(-38.29, 3) * mm, "mid": v(-42.29, 5) * mm, "end": v(-46.29, 3) * mm});
            skArc(sketch, "E96", {"start": v(-37.29, 0) * mm, "mid": v(-37.54, 1.58) * mm, "end": v(-38.29, 3) * mm});
            skSolve(sketch);
        }
        {
            var Q1;
            Q1=makeQuery(id+"F24.imprint","IMPRINT",FACE,{"disambiguationData":[TD([[makeQuery(id+"F24.imprint","IMPRINT",EDGE,{"derivedFrom":sQuery(id+"F24.wireOp",EDGE,"E91.0")}),1.0]])]});
            var Q2;
            Q2=makeQuery(id+"F23.imprint","IMPRINT",FACE,{"disambiguationData":[TD([[makeQuery(id+"F23.imprint","IMPRINT",EDGE,{"derivedFrom":sQuery(id+"F23.wireOp",EDGE,"E87.0")}),-1.0]])]});
            var Q3;
            Q3=makeQuery(id+"F22.boolean.opBoolean","SPLIT",EDGE,{"derivedFrom":makeQuery(id+"F3.opExtrude","CAP_EDGE",EDGE,{"disambiguationData":[OSD([sQuery(id+"F2.wireOp",EDGE,"E31.MirrorCS")])],"isStart":true})});
            loft(context, id + "F25", {"operationType" : NewBodyOperationType.ADD, "addGuides" : true, "sheetProfilesArray" : [{ "sheetProfileEntities" : qUnion([Q1]) }, { "sheetProfileEntities" : qUnion([Q2]) }], "guidesArray" : [{ "guideEntities" : qUnion([Q3]), "guideDerivativeType" : LoftGuideDerivativeType.DEFAULT, "guideDerivativeMagnitude" : 1 }]});
        }
        {
            var Q0;
            Q0=makeQuery(id+"F5.opExtrude","SWEPT_FACE",FACE,{"disambiguationData":[OSD([sQuery(id+"F4.wireOp",EDGE,"E43")])]});
            var sketch = newSketch(context, id + "F26", { "sketchPlane" : qUnion([Q0])});
            skLineSegment(sketch, "E97.0", {"start": v(43.56, -15) * mm, "end": v(35.53, -15) * mm});
            skLineSegment(sketch, "E98.0", {"start": v(35.53, -15) * mm, "end": v(35.53, 0) * mm});
            skLineSegment(sketch, "E99.0", {"start": v(43.56, -15) * mm, "end": v(43.56, 0) * mm});
            skLineSegment(sketch, "E100.0", {"start": v(43.56, 0) * mm, "end": v(35.53, 0) * mm});
            skSolve(sketch);
        }
        {
            var Q0;
            Q0=makeQuery(id+"F20.opSweep","CAP_FACE",FACE,{"disambiguationData":[OSD([sQuery(id+"F18.wireOp",VERTEX,"2932f9a6-44f9-4283-915d-18f9e60a3fe2.0.end"),sQuery(id+"F19.wireOp",EDGE,"E83"),sQuery(id+"F19.wireOp",EDGE,"E84")])],"isStart":false});
            var sketch = newSketch(context, id + "F27", { "sketchPlane" : qUnion([Q0])});
            skArc(sketch, "E101", {"start": v(38.29, 3) * mm, "mid": v(37.54, 1.58) * mm, "end": v(37.29, 0) * mm});
            skArc(sketch, "E102", {"start": v(46.29, 3) * mm, "mid": v(42.29, 5) * mm, "end": v(38.29, 3) * mm});
            skArc(sketch, "E103", {"start": v(47.29, 0) * mm, "mid": v(47.03, 1.58) * mm, "end": v(46.29, 3) * mm});
            skLineSegment(sketch, "E104", {"start": v(37.29, 0) * mm, "end": v(47.29, 0) * mm});
            skSolve(sketch);
        }
        {
            var Q1;
            Q1=makeQuery(id+"F27.imprint","IMPRINT",FACE,{"disambiguationData":[TD([[makeQuery(id+"F27.imprint","IMPRINT",EDGE,{"derivedFrom":sQuery(id+"F27.wireOp",EDGE,"E101")}),1.0]])]});
            var Q2;
            Q2=makeQuery(id+"F26.imprint","IMPRINT",FACE,{"disambiguationData":[TD([[makeQuery(id+"F26.imprint","IMPRINT",EDGE,{"derivedFrom":sQuery(id+"F26.wireOp",EDGE,"E97.0")}),-1.0]])]});
            var Q3;
            Q3=makeQuery(id+"F20.boolean.opBoolean","SPLIT",EDGE,{"derivedFrom":makeQuery(id+"F3.opExtrude","CAP_EDGE",EDGE,{"disambiguationData":[OSD([sQuery(id+"F2.wireOp",EDGE,"E26")])],"isStart":true})});
            loft(context, id + "F28", {"operationType" : NewBodyOperationType.ADD, "addGuides" : true, "sheetProfilesArray" : [{ "sheetProfileEntities" : qUnion([Q1]) }, { "sheetProfileEntities" : qUnion([Q2]) }], "guidesArray" : [{ "guideEntities" : qUnion([Q3]), "guideDerivativeType" : LoftGuideDerivativeType.DEFAULT, "guideDerivativeMagnitude" : 1 }]});
        }
        {
            var Q0;
            Q0=qCreatedBy(makeId("Front.planeOp"),FACE);
            var sketch = newSketch(context, id + "F29", { "sketchPlane" : qUnion([Q0])});
            skLineSegment(sketch, "E105", {"start": v(-45.1, 93.87) * mm, "end": v(46.3, 82.65) * mm});
            skLineSegment(sketch, "E106.MirrorCS", {"start": v(45.1, 93.87) * mm, "end": v(-46.3, 82.65) * mm});
            skPoint(sketch, "E107", {"position": v(41.3, 83.26) * mm});
            skPoint(sketch, "E108", {"position": v(-40.1, 93.25) * mm});
            skLineSegment(sketch, "E109", {"start": v(-40.1, 93.25) * mm, "end": v(41.3, 83.26) * mm, "construction": true});
            skSolve(sketch);
        }
        {
            var Q0;
            Q0=sQuery(id+"F29.wireOp",VERTEX,"E105.end");
            var Q1;
            Q1=qCreatedBy(makeId("Right.planeOp"),FACE);
            cPlane(context, id + "F30", {"entities" : qUnion([Q0, Q1]), "cplaneType" : CPlaneType.PLANE_POINT, "offset" : 25 * mm, "width" : 150 * mm, "height" : 150 * mm});
        }
        {
            var Q0;
            Q0=qCreatedBy(id+"F30.planeOp",FACE);
            var sketch = newSketch(context, id + "F31", { "sketchPlane" : qUnion([Q0])});
            skLineSegment(sketch, "E110.left", {"start": v(6.56, 79.47) * mm, "end": v(3.73, 82.3) * mm});
            skLineSegment(sketch, "E110.right", {"start": v(10.1, 83) * mm, "end": v(7.27, 85.83) * mm});
            skPoint(sketch, "E110.middle", {"position": v(6.91, 82.65) * mm});
            skArc(sketch, "E111", {"start": v(6.56, 79.47) * mm, "mid": v(10.1, 79.47) * mm, "end": v(10.1, 83) * mm});
            skArc(sketch, "E112", {"start": v(7.27, 85.83) * mm, "mid": v(3.73, 85.83) * mm, "end": v(3.73, 82.3) * mm});
            skPoint(sketch, "E113.0", {"position": v(-2.5, 130) * mm});
            skSolve(sketch);
        }
        {
            var Q0;
            Q0=makeQuery(id+"F31.imprint","IMPRINT",FACE,{"disambiguationData":[TD([[makeQuery(id+"F31.imprint","IMPRINT",EDGE,{"derivedFrom":sQuery(id+"F31.wireOp",EDGE,"E110.left")}),-1.0]])]});
            var Q1;
            Q1=sQuery(id+"F29.wireOp",EDGE,"E105");
            sweep(context, id + "F32", {"operationType" : NewBodyOperationType.REMOVE, "profiles" : qUnion([Q0]), "path" : qUnion([Q1])});
        }
        {
            var Q0;
            Q0=sQuery(id+"F29.wireOp",VERTEX,"E106.MirrorCS.start");
            var Q1;
            Q1=qCreatedBy(makeId("Right.planeOp"),FACE);
            cPlane(context, id + "F33", {"entities" : qUnion([Q0, Q1]), "cplaneType" : CPlaneType.PLANE_POINT, "offset" : 25 * mm, "width" : 150 * mm, "height" : 150 * mm});
        }
        {
            var Q0;
            Q0=qCreatedBy(id+"F33.planeOp",FACE);
            var sketch = newSketch(context, id + "F34", { "sketchPlane" : qUnion([Q0])});
            skLineSegment(sketch, "E114.left", {"start": v(7.27, 97.05) * mm, "end": v(10.1, 94.22) * mm});
            skLineSegment(sketch, "E114.right", {"start": v(3.73, 93.51) * mm, "end": v(6.56, 90.69) * mm});
            skPoint(sketch, "E114.middle", {"position": v(6.91, 93.87) * mm});
            skArc(sketch, "E115", {"start": v(7.27, 97.05) * mm, "mid": v(3.73, 97.05) * mm, "end": v(3.73, 93.51) * mm});
            skArc(sketch, "E116", {"start": v(6.56, 90.69) * mm, "mid": v(10.1, 90.69) * mm, "end": v(10.1, 94.22) * mm});
            skPoint(sketch, "E117.0", {"position": v(-2.87, 141.57) * mm});
            skSolve(sketch);
        }
        {
            var Q0;
            Q0=makeQuery(id+"F34.imprint","IMPRINT",FACE,{"disambiguationData":[TD([[makeQuery(id+"F34.imprint","IMPRINT",EDGE,{"derivedFrom":sQuery(id+"F34.wireOp",EDGE,"E114.left")}),-1.0]])]});
            var Q1;
            Q1=sQuery(id+"F29.wireOp",EDGE,"E106.MirrorCS");
            sweep(context, id + "F35", {"operationType" : NewBodyOperationType.REMOVE, "profiles" : qUnion([Q0]), "path" : qUnion([Q1])});
        }
        {
            var Q0;
            Q0=makeQuery(id+"F25.boolean.opBoolean","MERGE",EDGE,{"derivedFrom":[makeQuery(id+"F5.opExtrude","CAP_EDGE",EDGE,{"disambiguationData":[OSD([sQuery(id+"F4.wireOp",EDGE,"E44")])],"isStart":false}),makeQuery(id+"F25.opLoft","MID_CAP_EDGE",EDGE,{"disambiguationData":[OSD([sQuery(id+"F23.wireOp",EDGE,"E87.0"),sQuery(id+"F23.wireOp",EDGE,"E88.0"),sQuery(id+"F23.wireOp",EDGE,"E89.0")])],"capPos":1.0})]});
            var Q1;
            Q1=makeQuery(id+"F25.boolean.opBoolean","MERGE",EDGE,{"derivedFrom":[makeQuery(id+"F5.opExtrude","SWEPT_EDGE",EDGE,{"disambiguationData":[OSD([sQuery(id+"F4.wireOp",EDGE,"E40.0"),sQuery(id+"F4.wireOp",EDGE,"E44")])]}),makeQuery(id+"F25.opLoft","MID_CAP_EDGE",EDGE,{"disambiguationData":[OSD([sQuery(id+"F23.wireOp",EDGE,"E87.0"),sQuery(id+"F23.wireOp",EDGE,"E89.0"),sQuery(id+"F23.wireOp",EDGE,"E90")])],"capPos":1.0})]});
            var Q2;
            Q2=makeQuery(id+"F28.boolean.opBoolean","MERGE",EDGE,{"derivedFrom":[makeQuery(id+"F5.opExtrude","CAP_EDGE",EDGE,{"disambiguationData":[OSD([sQuery(id+"F4.wireOp",EDGE,"E43")])],"isStart":false}),makeQuery(id+"F28.opLoft","MID_CAP_EDGE",EDGE,{"disambiguationData":[OSD([sQuery(id+"F26.wireOp",EDGE,"E97.0"),sQuery(id+"F26.wireOp",EDGE,"E98.0"),sQuery(id+"F26.wireOp",EDGE,"E99.0")])],"capPos":1.0})]});
            var Q3;
            Q3=makeQuery(id+"F28.boolean.opBoolean","MERGE",EDGE,{"derivedFrom":[makeQuery(id+"F5.opExtrude","SWEPT_EDGE",EDGE,{"disambiguationData":[OSD([sQuery(id+"F4.wireOp",EDGE,"E39.0"),sQuery(id+"F4.wireOp",EDGE,"E43")])]}),makeQuery(id+"F28.opLoft","MID_CAP_EDGE",EDGE,{"disambiguationData":[OSD([sQuery(id+"F26.wireOp",EDGE,"E97.0"),sQuery(id+"F26.wireOp",EDGE,"E98.0"),sQuery(id+"F26.wireOp",EDGE,"E100.0")])],"capPos":1.0})]});
            fillet(context, id + "F36", {"entities" : qUnion([Q0, Q1, Q2, Q3]), "radius" : 10 * mm, "tangentPropagation" : true, "allowEdgeOverflow" : false});
        }
        {
            var Q0;
            Q0=makeQuery(id+"F28.boolean.opBoolean","MERGE",EDGE,{"derivedFrom":[makeQuery(id+"F20.opSweep","CAP_EDGE",EDGE,{"disambiguationData":[OSD([sQuery(id+"F18.wireOp",VERTEX,"2932f9a6-44f9-4283-915d-18f9e60a3fe2.0.end"),sQuery(id+"F19.wireOp",EDGE,"E83")])],"isStart":false}),makeQuery(id+"F28.opLoft","MID_CAP_EDGE",EDGE,{"disambiguationData":[OSD([sQuery(id+"F27.wireOp",EDGE,"E101"),sQuery(id+"F27.wireOp",EDGE,"E102"),sQuery(id+"F27.wireOp",EDGE,"E103")])],"capPos":0.0})]});
            var Q1;
            Q1=makeQuery(id+"F25.boolean.opBoolean","MERGE",EDGE,{"derivedFrom":[makeQuery(id+"F22.opSweep","CAP_EDGE",EDGE,{"disambiguationData":[OSD([sQuery(id+"F18.wireOp",VERTEX,"E81.0.end"),sQuery(id+"F21.wireOp",EDGE,"E85")])],"isStart":false}),makeQuery(id+"F25.opLoft","MID_CAP_EDGE",EDGE,{"disambiguationData":[OSD([sQuery(id+"F24.wireOp",EDGE,"E94"),sQuery(id+"F24.wireOp",EDGE,"E95"),sQuery(id+"F24.wireOp",EDGE,"E96")])],"capPos":0.0})]});
            var Q2;
            Q2=makeQuery(id+"F28.boolean.opBoolean","MERGE",EDGE,{"derivedFrom":[makeQuery(id+"F20.opSweep","CAP_EDGE",EDGE,{"disambiguationData":[OSD([sQuery(id+"F18.wireOp",VERTEX,"2932f9a6-44f9-4283-915d-18f9e60a3fe2.0.end"),sQuery(id+"F19.wireOp",EDGE,"E83")])],"isStart":false}),makeQuery(id+"F28.opLoft","MID_CAP_EDGE",EDGE,{"disambiguationData":[OSD([sQuery(id+"F27.wireOp",EDGE,"E101"),sQuery(id+"F27.wireOp",EDGE,"E102"),sQuery(id+"F27.wireOp",EDGE,"E104")])],"capPos":0.0})]});
            var Q3;
            Q3=makeQuery(id+"F25.boolean.opBoolean","MERGE",EDGE,{"derivedFrom":[makeQuery(id+"F22.opSweep","CAP_EDGE",EDGE,{"disambiguationData":[OSD([sQuery(id+"F18.wireOp",VERTEX,"E81.0.end"),sQuery(id+"F21.wireOp",EDGE,"E85")])],"isStart":false}),makeQuery(id+"F25.opLoft","MID_CAP_EDGE",EDGE,{"disambiguationData":[OSD([sQuery(id+"F24.wireOp",EDGE,"E91.0"),sQuery(id+"F24.wireOp",EDGE,"E95"),sQuery(id+"F24.wireOp",EDGE,"E96")])],"capPos":0.0})]});
            fillet(context, id + "F37", {"entities" : qUnion([Q0, Q1, Q2, Q3]), "radius" : 5 * mm, "tangentPropagation" : true, "allowEdgeOverflow" : false});
        }
        {
            var Q0;
            Q0=makeQuery(id+"F5.opExtrude","CAP_EDGE",EDGE,{"disambiguationData":[OSD([sQuery(id+"F4.wireOp",EDGE,"E41")])],"isStart":false});
            fillet(context, id + "F38", {"entities" : qUnion([Q0]), "radius" : 2 * mm, "tangentPropagation" : true, "allowEdgeOverflow" : false});
        }
        {
            var Q0;
            Q0=makeQuery(id+"F22.boolean.opBoolean","MERGE",FACE,{"derivedFrom":[makeQuery(id+"F20.boolean.opBoolean","MERGE",FACE,{"derivedFrom":[makeQuery(id+"F3.opExtrude","SWEPT_FACE",FACE,{"disambiguationData":[OSD([sQuery(id+"F2.wireOp",EDGE,"E1"),sQuery(id+"F2.wireOp",EDGE,"E2"),sQuery(id+"F2.wireOp",EDGE,"E27")])]}),makeQuery(id+"F20.opSweep","CAP_FACE",FACE,{"disambiguationData":[OSD([sQuery(id+"F18.wireOp",VERTEX,"E82.0.start"),sQuery(id+"F19.wireOp",EDGE,"E83"),sQuery(id+"F19.wireOp",EDGE,"E84")])],"isStart":true})]}),makeQuery(id+"F22.opSweep","CAP_FACE",FACE,{"disambiguationData":[OSD([sQuery(id+"F18.wireOp",VERTEX,"E81.0.start"),sQuery(id+"F21.wireOp",EDGE,"E85"),sQuery(id+"F21.wireOp",EDGE,"E86")])],"isStart":true})]});
            var sketch = newSketch(context, id + "F39", { "sketchPlane" : qUnion([Q0])});
            skLineSegment(sketch, "E118", {"start": v(36, 0) * mm, "end": v(18, 0) * mm, "construction": true});
            skLineSegment(sketch, "E119", {"start": v(18, 0) * mm, "end": v(0, 0) * mm, "construction": true});
            skLineSegment(sketch, "E120", {"start": v(0, 0) * mm, "end": v(-18, 0) * mm, "construction": true});
            skLineSegment(sketch, "E121", {"start": v(-18, 0) * mm, "end": v(-36, 0) * mm, "construction": true});
            skArc(sketch, "E122", {"start": v(26, 0) * mm, "mid": v(28.5, -2.5) * mm, "end": v(31, 0) * mm});
            skLineSegment(sketch, "E123", {"start": v(31, 0) * mm, "end": v(26, 0) * mm});
            skArc(sketch, "E124", {"start": v(5, 0) * mm, "mid": v(7.5, -2.5) * mm, "end": v(10, 0) * mm});
            skLineSegment(sketch, "E125", {"start": v(10, 0) * mm, "end": v(5, 0) * mm});
            skArc(sketch, "E126", {"start": v(-2.5, 0) * mm, "mid": v(0, -2.5) * mm, "end": v(2.5, 0) * mm});
            skLineSegment(sketch, "E127", {"start": v(2.5, 0) * mm, "end": v(-2.5, 0) * mm});
            skArc(sketch, "E128", {"start": v(-10, 0) * mm, "mid": v(-7.5, -2.5) * mm, "end": v(-5, 0) * mm});
            skLineSegment(sketch, "E129", {"start": v(-5, 0) * mm, "end": v(-10, 0) * mm});
            skArc(sketch, "E130", {"start": v(-31, 0) * mm, "mid": v(-28.5, -2.5) * mm, "end": v(-26, 0) * mm});
            skLineSegment(sketch, "E131", {"start": v(-31, 0) * mm, "end": v(-26, 0) * mm});
            skSolve(sketch);
        }
        {
            var Q0;
            Q0 = qSketchRegion(id + "F39", true);
            extrude(context, id + "F40", {"entities" : qUnion([Q0]), "operationType" : NewBodyOperationType.ADD, "endBound" : BoundingType.UP_TO_NEXT, "oppositeDirection" : true, "depth" : 25 * mm});
        }
        {
            var Q0;
            {var subQ0=sQuery(id+"F39.wireOp",EDGE,"E128");var subQ1=makeQuery(id+"F40.opExtrude","CAP_FACE",FACE,{"disambiguationData":[OSD([subQ0,sQuery(id+"F39.wireOp",EDGE,"E129")])],"isStart":true});var subQ2=sQuery(id+"F39.wireOp",EDGE,"E124");var subQ3=makeQuery(id+"F40.opExtrude","CAP_FACE",FACE,{"disambiguationData":[OSD([subQ2,sQuery(id+"F39.wireOp",EDGE,"E125")])],"isStart":true});var subQ4=makeQuery(id+"F40.opExtrude","SWEPT_FACE",FACE,{"disambiguationData":[OSD([subQ0])]});var subQ5=sQuery(id+"F39.wireOp",EDGE,"E122");var subQ6=makeQuery(id+"F40.opExtrude","CAP_FACE",FACE,{"disambiguationData":[OSD([subQ5,sQuery(id+"F39.wireOp",EDGE,"E123")])],"isStart":true});var subQ7=sQuery(id+"F39.wireOp",EDGE,"E126");var subQ8=makeQuery(id+"F40.opExtrude","CAP_FACE",FACE,{"disambiguationData":[OSD([subQ7,sQuery(id+"F39.wireOp",EDGE,"E127")])],"isStart":true});var subQ9=sQuery(id+"F2.wireOp",EDGE,"E27");var subQ10=sQuery(id+"F2.wireOp",EDGE,"E2");var subQ11=sQuery(id+"F2.wireOp",EDGE,"E1");var subQ12=makeQuery(id+"F3.opExtrude","SWEPT_FACE",FACE,{"disambiguationData":[OSD([subQ11,subQ10,subQ9])]});var subQ13=makeQuery(id+"F22.opSweep","CAP_FACE",FACE,{"disambiguationData":[OSD([sQuery(id+"F18.wireOp",VERTEX,"E81.0.start"),sQuery(id+"F21.wireOp",EDGE,"E85"),sQuery(id+"F21.wireOp",EDGE,"E86")])],"isStart":true});var subQ14=makeQuery(id+"F20.opSweep","CAP_FACE",FACE,{"disambiguationData":[OSD([sQuery(id+"F18.wireOp",VERTEX,"E82.0.start"),sQuery(id+"F19.wireOp",EDGE,"E83"),sQuery(id+"F19.wireOp",EDGE,"E84")])],"isStart":true});var subQ15=makeQuery(id+"F5.opExtrude","SWEPT_FACE",FACE,{"disambiguationData":[OSD([sQuery(id+"F4.wireOp",EDGE,"E41")])]});var subQ16=makeQuery(id+"F40.opExtrude","SWEPT_FACE",FACE,{"disambiguationData":[OSD([subQ7])]});var subQ17=sQuery(id+"F39.wireOp",EDGE,"E130");var subQ18=makeQuery(id+"F40.opExtrude","CAP_FACE",FACE,{"disambiguationData":[OSD([subQ17,sQuery(id+"F39.wireOp",EDGE,"E131")])],"isStart":true});var subQ19=makeQuery(id+"F3.opExtrude","CAP_FACE",FACE,{"disambiguationData":[OSD([subQ11,subQ10,sQuery(id+"F2.wireOp",EDGE,"E15"),sQuery(id+"F2.wireOp",EDGE,"E26"),subQ9,sQuery(id+"F2.wireOp",EDGE,"E30.MirrorCS"),sQuery(id+"F2.wireOp",EDGE,"E31.MirrorCS")])],"isStart":true});var subQ20=makeQuery(id+"F40.opExtrude","SWEPT_FACE",FACE,{"disambiguationData":[OSD([subQ2])]});Q0=qUnion([makeQuery(id+"F40.boolean.opBoolean","SPLIT",FACE,{"disambiguationData":[TD([subQ12,subQ15,subQ14,subQ13,subQ6,subQ20,subQ3,subQ16,subQ8,subQ1,subQ18])],"derivedFrom":subQ19}),makeQuery(id+"F40.boolean.opBoolean","SPLIT",FACE,{"disambiguationData":[TD([subQ12,subQ15,subQ14,subQ13,subQ6,subQ3,subQ8,subQ4,subQ1,makeQuery(id+"F40.opExtrude","SWEPT_FACE",FACE,{"disambiguationData":[OSD([subQ17])]}),subQ18])],"derivedFrom":subQ19}),makeQuery(id+"F40.boolean.opBoolean","SPLIT",FACE,{"disambiguationData":[TD([subQ12,subQ15,subQ14,subQ13,makeQuery(id+"F40.opExtrude","SWEPT_FACE",FACE,{"disambiguationData":[OSD([subQ5])]}),subQ6,subQ20,subQ3,subQ8,subQ1,subQ18])],"derivedFrom":subQ19}),makeQuery(id+"F40.boolean.opBoolean","SPLIT",FACE,{"disambiguationData":[TD([subQ12,subQ15,subQ14,subQ13,subQ6,subQ3,subQ16,subQ8,subQ4,subQ1,subQ18])],"derivedFrom":subQ19})]);}
            var sketch = newSketch(context, id + "F41", { "sketchPlane" : qUnion([Q0])});
            skCircle(sketch, "E132", {"center": v(-18, 15) * mm, "radius": 3 * mm});
            skLineSegment(sketch, "E133", {"start": v(-26, 0) * mm, "end": v(-10, 0) * mm, "construction": true});
            skPoint(sketch, "E134", {"position": v(-18, 0) * mm});
            skCircle(sketch, "E135.0.1.0", {"center": v(-18, 45) * mm, "radius": 3 * mm});
            skLineSegment(sketch, "E135.direction1", {"start": v(-18, 15) * mm, "end": v(7, 15) * mm, "construction": true});
            skLineSegment(sketch, "E135.direction2", {"start": v(-18, 15) * mm, "end": v(-18, 45) * mm, "construction": true});
            skCircle(sketch, "E136.MirrorC", {"center": v(18, 15) * mm, "radius": 3 * mm});
            skCircle(sketch, "E137.MirrorC", {"center": v(18, 45) * mm, "radius": 3 * mm});
            skLineSegment(sketch, "E138.MirrorCS", {"start": v(18, 15) * mm, "end": v(18, 45) * mm, "construction": true});
            skSolve(sketch);
        }
        {
            var Q0;
            Q0 = qSketchRegion(id + "F41", true);
            extrude(context, id + "F42", {"entities" : qUnion([Q0]), "operationType" : NewBodyOperationType.REMOVE, "oppositeDirection" : true, "depth" : 25 * mm});
        }
        {
            var Q0;
            {var subQ0=sQuery(id+"F6.wireOp",EDGE,"E46.0");Q0=makeQuery(id+"F7.boolean.opBoolean","MERGE",FACE,{"derivedFrom":[makeQuery(id+"F3.opExtrude","CAP_FACE",FACE,{"disambiguationData":[OSD([sQuery(id+"F2.wireOp",EDGE,"E1"),sQuery(id+"F2.wireOp",EDGE,"E2"),sQuery(id+"F2.wireOp",EDGE,"E15"),sQuery(id+"F2.wireOp",EDGE,"E26"),sQuery(id+"F2.wireOp",EDGE,"E27"),sQuery(id+"F2.wireOp",EDGE,"E30.MirrorCS"),sQuery(id+"F2.wireOp",EDGE,"E31.MirrorCS")])],"isStart":false}),makeQuery(id+"F7.opExtrude","CAP_FACE",FACE,{"disambiguationData":[OSD([subQ0,sQuery(id+"F6.wireOp",EDGE,"E54.MirrorCS"),sQuery(id+"F6.wireOp",EDGE,"E55.MirrorCS"),sQuery(id+"F6.wireOp",EDGE,"E59")])],"isStart":false}),makeQuery(id+"F7.opExtrude","CAP_FACE",FACE,{"disambiguationData":[OSD([subQ0,sQuery(id+"F6.wireOp",EDGE,"E50"),sQuery(id+"F6.wireOp",EDGE,"E51"),sQuery(id+"F6.wireOp",EDGE,"E60.MirrorCS")])],"isStart":false})]});}
            var sketch = newSketch(context, id + "F43", { "sketchPlane" : qUnion([Q0])});
            skLineSegment(sketch, "E139", {"start": v(-46, 0) * mm, "end": v(-15.33, 0) * mm, "construction": true});
            skLineSegment(sketch, "E140", {"start": v(-15.33, 0) * mm, "end": v(15.33, 0) * mm, "construction": true});
            skLineSegment(sketch, "E141", {"start": v(15.33, 0) * mm, "end": v(46, 0) * mm, "construction": true});
            skPoint(sketch, "E142", {"position": v(0, 0) * mm});
            skPoint(sketch, "E143", {"position": v(-30.67, 0) * mm});
            skPoint(sketch, "E144", {"position": v(30.67, 0) * mm});
            skLineSegment(sketch, "E145.bottom", {"start": v(-28.17, 15) * mm, "end": v(-33.17, 15) * mm});
            skLineSegment(sketch, "E145.top", {"start": v(-28.17, 10) * mm, "end": v(-33.17, 10) * mm});
            skLineSegment(sketch, "E145.left", {"start": v(-28.17, 15) * mm, "end": v(-28.17, 10) * mm});
            skLineSegment(sketch, "E145.right", {"start": v(-33.17, 15) * mm, "end": v(-33.17, 10) * mm});
            skPoint(sketch, "E145.middle", {"position": v(-30.67, 12.5) * mm});
            skPoint(sketch, "E146.0.1.0", {"position": v(-30.67, 32.5) * mm});
            skLineSegment(sketch, "E146.0.1.1", {"start": v(-28.17, 30) * mm, "end": v(-33.17, 30) * mm});
            skLineSegment(sketch, "E146.0.1.2", {"start": v(-28.17, 35) * mm, "end": v(-33.17, 35) * mm});
            skLineSegment(sketch, "E146.0.1.3", {"start": v(-33.17, 35) * mm, "end": v(-33.17, 30) * mm});
            skLineSegment(sketch, "E146.0.1.4", {"start": v(-28.17, 35) * mm, "end": v(-28.17, 30) * mm});
            skPoint(sketch, "E146.0.2.0", {"position": v(-30.67, 52.5) * mm});
            skLineSegment(sketch, "E146.0.2.1", {"start": v(-28.17, 50) * mm, "end": v(-33.17, 50) * mm});
            skLineSegment(sketch, "E146.0.2.2", {"start": v(-28.17, 55) * mm, "end": v(-33.17, 55) * mm});
            skLineSegment(sketch, "E146.0.2.3", {"start": v(-33.17, 55) * mm, "end": v(-33.17, 50) * mm});
            skLineSegment(sketch, "E146.0.2.4", {"start": v(-28.17, 55) * mm, "end": v(-28.17, 50) * mm});
            skPoint(sketch, "E146.0.3.0", {"position": v(-30.67, 72.5) * mm});
            skLineSegment(sketch, "E146.0.3.1", {"start": v(-28.17, 70) * mm, "end": v(-33.17, 70) * mm});
            skLineSegment(sketch, "E146.0.3.2", {"start": v(-28.17, 75) * mm, "end": v(-33.17, 75) * mm});
            skLineSegment(sketch, "E146.0.3.3", {"start": v(-33.17, 75) * mm, "end": v(-33.17, 70) * mm});
            skLineSegment(sketch, "E146.0.3.4", {"start": v(-28.17, 75) * mm, "end": v(-28.17, 70) * mm});
            skPoint(sketch, "E146.1.0.0", {"position": v(0, 12.5) * mm});
            skLineSegment(sketch, "E146.1.0.1", {"start": v(2.5, 10) * mm, "end": v(-2.5, 10) * mm});
            skLineSegment(sketch, "E146.1.0.2", {"start": v(2.5, 15) * mm, "end": v(-2.5, 15) * mm});
            skLineSegment(sketch, "E146.1.0.3", {"start": v(-2.5, 15) * mm, "end": v(-2.5, 10) * mm});
            skLineSegment(sketch, "E146.1.0.4", {"start": v(2.5, 15) * mm, "end": v(2.5, 10) * mm});
            skPoint(sketch, "E146.1.1.0", {"position": v(0, 32.5) * mm});
            skLineSegment(sketch, "E146.1.1.1", {"start": v(2.5, 30) * mm, "end": v(-2.5, 30) * mm});
            skLineSegment(sketch, "E146.1.1.2", {"start": v(2.5, 35) * mm, "end": v(-2.5, 35) * mm});
            skLineSegment(sketch, "E146.1.1.3", {"start": v(-2.5, 35) * mm, "end": v(-2.5, 30) * mm});
            skLineSegment(sketch, "E146.1.1.4", {"start": v(2.5, 35) * mm, "end": v(2.5, 30) * mm});
            skPoint(sketch, "E146.1.2.0", {"position": v(0, 52.5) * mm});
            skLineSegment(sketch, "E146.1.2.1", {"start": v(2.5, 50) * mm, "end": v(-2.5, 50) * mm});
            skLineSegment(sketch, "E146.1.2.2", {"start": v(2.5, 55) * mm, "end": v(-2.5, 55) * mm});
            skLineSegment(sketch, "E146.1.2.3", {"start": v(-2.5, 55) * mm, "end": v(-2.5, 50) * mm});
            skLineSegment(sketch, "E146.1.2.4", {"start": v(2.5, 55) * mm, "end": v(2.5, 50) * mm});
            skPoint(sketch, "E146.1.3.0", {"position": v(0, 72.5) * mm});
            skLineSegment(sketch, "E146.1.3.1", {"start": v(2.5, 70) * mm, "end": v(-2.5, 70) * mm});
            skLineSegment(sketch, "E146.1.3.2", {"start": v(2.5, 75) * mm, "end": v(-2.5, 75) * mm});
            skLineSegment(sketch, "E146.1.3.3", {"start": v(-2.5, 75) * mm, "end": v(-2.5, 70) * mm});
            skLineSegment(sketch, "E146.1.3.4", {"start": v(2.5, 75) * mm, "end": v(2.5, 70) * mm});
            skPoint(sketch, "E146.2.0.0", {"position": v(30.67, 12.5) * mm});
            skLineSegment(sketch, "E146.2.0.1", {"start": v(33.17, 10) * mm, "end": v(28.17, 10) * mm});
            skLineSegment(sketch, "E146.2.0.2", {"start": v(33.17, 15) * mm, "end": v(28.17, 15) * mm});
            skLineSegment(sketch, "E146.2.0.3", {"start": v(28.17, 15) * mm, "end": v(28.17, 10) * mm});
            skLineSegment(sketch, "E146.2.0.4", {"start": v(33.17, 15) * mm, "end": v(33.17, 10) * mm});
            skPoint(sketch, "E146.2.1.0", {"position": v(30.67, 32.5) * mm});
            skLineSegment(sketch, "E146.2.1.1", {"start": v(33.17, 30) * mm, "end": v(28.17, 30) * mm});
            skLineSegment(sketch, "E146.2.1.2", {"start": v(33.17, 35) * mm, "end": v(28.17, 35) * mm});
            skLineSegment(sketch, "E146.2.1.3", {"start": v(28.17, 35) * mm, "end": v(28.17, 30) * mm});
            skLineSegment(sketch, "E146.2.1.4", {"start": v(33.17, 35) * mm, "end": v(33.17, 30) * mm});
            skPoint(sketch, "E146.2.2.0", {"position": v(30.67, 52.5) * mm});
            skLineSegment(sketch, "E146.2.2.1", {"start": v(33.17, 50) * mm, "end": v(28.17, 50) * mm});
            skLineSegment(sketch, "E146.2.2.2", {"start": v(33.17, 55) * mm, "end": v(28.17, 55) * mm});
            skLineSegment(sketch, "E146.2.2.3", {"start": v(28.17, 55) * mm, "end": v(28.17, 50) * mm});
            skLineSegment(sketch, "E146.2.2.4", {"start": v(33.17, 55) * mm, "end": v(33.17, 50) * mm});
            skPoint(sketch, "E146.2.3.0", {"position": v(30.67, 72.5) * mm});
            skLineSegment(sketch, "E146.2.3.1", {"start": v(33.17, 70) * mm, "end": v(28.17, 70) * mm});
            skLineSegment(sketch, "E146.2.3.2", {"start": v(33.17, 75) * mm, "end": v(28.17, 75) * mm});
            skLineSegment(sketch, "E146.2.3.3", {"start": v(28.17, 75) * mm, "end": v(28.17, 70) * mm});
            skLineSegment(sketch, "E146.2.3.4", {"start": v(33.17, 75) * mm, "end": v(33.17, 70) * mm});
            skLineSegment(sketch, "E146.direction1", {"start": v(-33.17, 10) * mm, "end": v(-2.5, 10) * mm, "construction": true});
            skLineSegment(sketch, "E146.direction2", {"start": v(-33.17, 10) * mm, "end": v(-33.17, 30) * mm, "construction": true});
            skLineSegment(sketch, "E147", {"start": v(-28.17, 75) * mm, "end": v(-2.5, 75) * mm, "construction": true});
            skLineSegment(sketch, "E148", {"start": v(2.5, 75) * mm, "end": v(28.17, 75) * mm, "construction": true});
            skPoint(sketch, "E149", {"position": v(-15.33, 75) * mm});
            skPoint(sketch, "E150", {"position": v(15.33, 75) * mm});
            skPoint(sketch, "E151.0.0.4", {"position": v(-30.67, 92.5) * mm});
            skLineSegment(sketch, "E151.1.0.4", {"start": v(-28.17, 90) * mm, "end": v(-33.17, 90) * mm});
            skLineSegment(sketch, "E151.4.0.4", {"start": v(-28.17, 95) * mm, "end": v(-33.17, 95) * mm});
            skLineSegment(sketch, "E151.7.0.4", {"start": v(-33.17, 95) * mm, "end": v(-33.17, 90) * mm});
            skLineSegment(sketch, "E151.10.0.4", {"start": v(-28.17, 95) * mm, "end": v(-28.17, 90) * mm});
            skPoint(sketch, "E151.0.1.4", {"position": v(0, 92.5) * mm});
            skLineSegment(sketch, "E151.1.1.4", {"start": v(2.5, 90) * mm, "end": v(-2.5, 90) * mm});
            skLineSegment(sketch, "E151.4.1.4", {"start": v(2.5, 95) * mm, "end": v(-2.5, 95) * mm});
            skLineSegment(sketch, "E151.7.1.4", {"start": v(-2.5, 95) * mm, "end": v(-2.5, 90) * mm});
            skLineSegment(sketch, "E151.10.1.4", {"start": v(2.5, 95) * mm, "end": v(2.5, 90) * mm});
            skPoint(sketch, "E151.0.2.4", {"position": v(30.67, 92.5) * mm});
            skLineSegment(sketch, "E151.1.2.4", {"start": v(33.17, 90) * mm, "end": v(28.17, 90) * mm});
            skLineSegment(sketch, "E151.4.2.4", {"start": v(33.17, 95) * mm, "end": v(28.17, 95) * mm});
            skLineSegment(sketch, "E151.7.2.4", {"start": v(28.17, 95) * mm, "end": v(28.17, 90) * mm});
            skLineSegment(sketch, "E151.10.2.4", {"start": v(33.17, 95) * mm, "end": v(33.17, 90) * mm});
            skSolve(sketch);
        }
        {
            var Q0;
            Q0 = qSketchRegion(id + "F43", true);
            extrude(context, id + "F44", {"entities" : qUnion([Q0]), "operationType" : NewBodyOperationType.ADD, "depth" : 25 * mm, "hasDraft" : true, "draftAngle" : 45 * degree, "draftPullDirection" : true});
        }
    });
